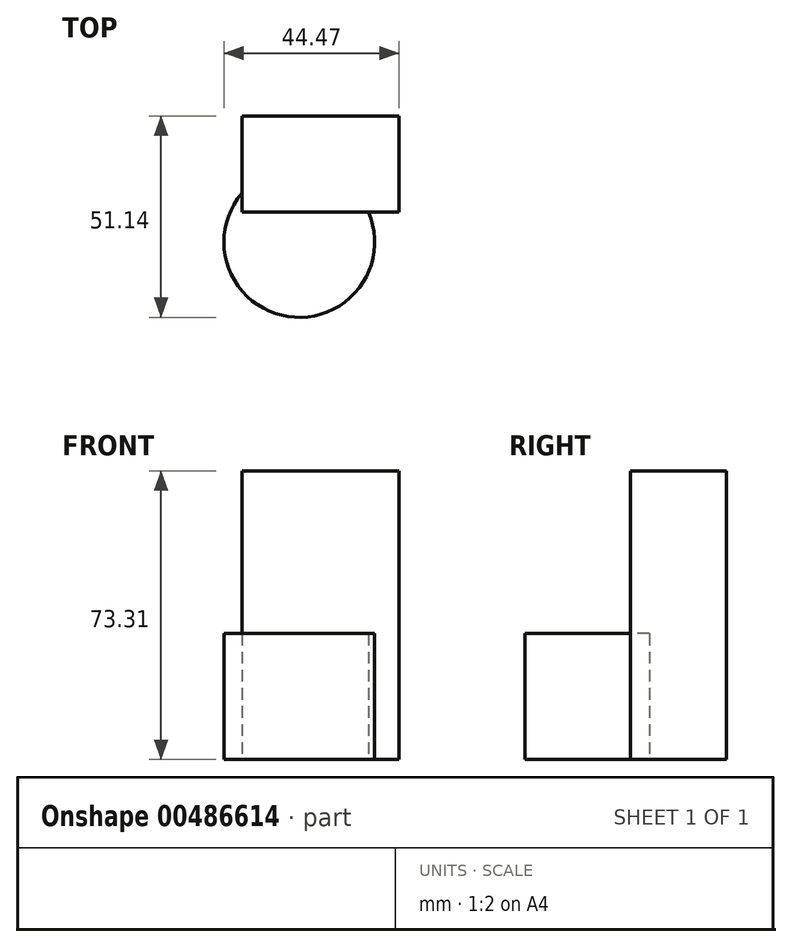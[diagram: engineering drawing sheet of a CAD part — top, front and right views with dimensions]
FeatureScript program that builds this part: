
annotation { "Feature Type Name" : "Feature", "Feature Type Description" : "" }
export const myFeature = defineFeature(function(context is Context, id is Id, definition is map)
    precondition{}
    {
        {
            var Q0;
            Q0=qCreatedBy(makeId("Top.planeOp"),FACE);
            var sketch = newSketch(context, id + "F0", { "sketchPlane" : qUnion([Q0])});
            skCircle(sketch, "E0", {"center": v(-36.23, 0) * mm, "radius": 19.15 * mm});
            skSolve(sketch);
        }
        {
            var Q0;
            Q0=makeQuery(id+"F0.imprint","IMPRINT",FACE,{"disambiguationData":[TD([[makeQuery(id+"F0.imprint","IMPRINT",EDGE,{"derivedFrom":sQuery(id+"F0.wireOp",EDGE,"E0")}),1.0]])]});
            extrude(context, id + "F1", {"entities" : qUnion([Q0]), "depth" : 31.96 * mm});
        }
        {
            var Q0;
            Q0=qCreatedBy(makeId("Top.planeOp"),FACE);
            var sketch = newSketch(context, id + "F2", { "sketchPlane" : qUnion([Q0])});
            skLineSegment(sketch, "E1.bottom", {"start": v(-50.8, 7.6) * mm, "end": v(-10.9, 7.6) * mm});
            skLineSegment(sketch, "E1.top", {"start": v(-50.8, 32) * mm, "end": v(-10.9, 32) * mm});
            skLineSegment(sketch, "E1.left", {"start": v(-50.8, 7.6) * mm, "end": v(-50.8, 32) * mm});
            skLineSegment(sketch, "E1.right", {"start": v(-10.9, 7.6) * mm, "end": v(-10.9, 32) * mm});
            skSolve(sketch);
        }
        {
            var Q0;
            Q0 = qSketchRegion(id + "F2", true);
            extrude(context, id + "F3", {"entities" : qUnion([Q0]), "operationType" : NewBodyOperationType.ADD, "depth" : 73.3 * mm});
        }
    });
